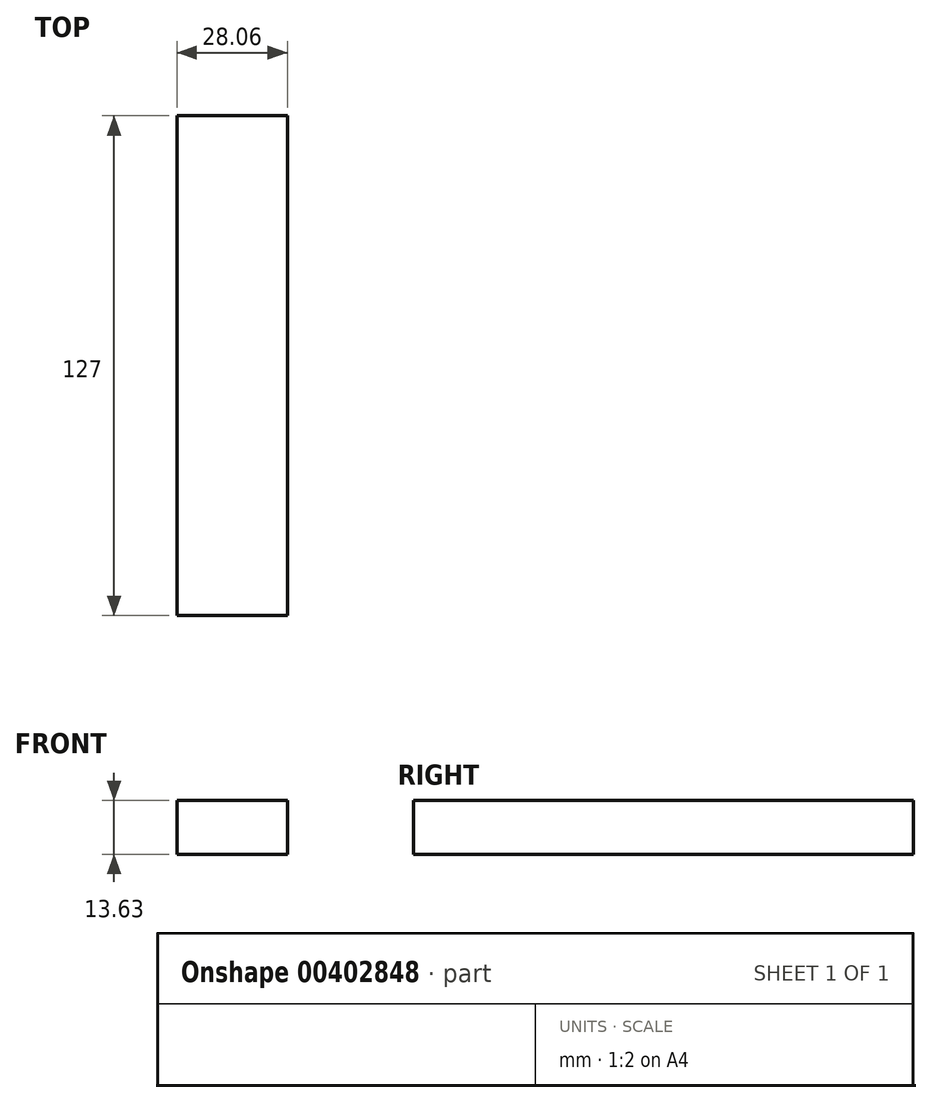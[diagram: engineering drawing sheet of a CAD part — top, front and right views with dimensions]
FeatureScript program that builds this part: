
annotation { "Feature Type Name" : "Feature", "Feature Type Description" : "" }
export const myFeature = defineFeature(function(context is Context, id is Id, definition is map)
    precondition{}
    {
        {
            var Q0;
            Q0=qCreatedBy(makeId("Front.planeOp"),FACE);
            var sketch = newSketch(context, id + "F0", { "sketchPlane" : qUnion([Q0])});
            skLineSegment(sketch, "E0.bottom", {"start": v(-26.3, 34.37) * mm, "end": v(1.75, 34.37) * mm});
            skLineSegment(sketch, "E0.top", {"start": v(-26.3, 20.74) * mm, "end": v(1.75, 20.74) * mm});
            skLineSegment(sketch, "E0.left", {"start": v(-26.3, 34.37) * mm, "end": v(-26.3, 20.74) * mm});
            skLineSegment(sketch, "E0.right", {"start": v(1.75, 34.37) * mm, "end": v(1.75, 20.74) * mm});
            skSolve(sketch);
        }
        {
            var Q0;
            Q0 = qSketchRegion(id + "F0", true);
            extrude(context, id + "F1", {"entities" : qUnion([Q0]), "depth" : 127 * mm});
        }
    });
